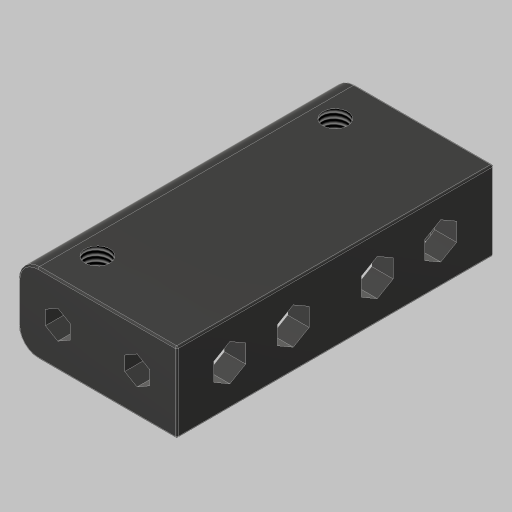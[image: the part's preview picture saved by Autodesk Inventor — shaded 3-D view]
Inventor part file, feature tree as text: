
AUTODESK INVENTOR PART (.ipt)
format: ipt  version: 2023.5 (Build 275446000, 446)  size: 305,664 bytes
history: native  units: in
note: dims shown in document units (in); Inventor stores cm internally (conversion verified against a paired STEP export)
features: sketch x5, extrude x4, fillet x3, projected_geometry x2, hole x1
ambient origin geometry x8: Origin, YZ Plane, XZ Plane, XY Plane, X Axis, Y Axis, Z Axis, Center Point
bodies: Solid1 (feature_tree)
feature tree (15):
  extrude  "Extrusion1"  Depth=0.5in
  hole  "Hole1"  [1 undecoded]
  fillet  "Fillet1"  Radius=0.25in
  fillet  "Fillet2"  Radius=0.125in
  extrude  "Extrusion2"  Depth=0.125in
  fillet  "Fillet3"  Radius=0.125in
  extrude  "Extrusion3"  Depth=0.375in TaperAngle=0.0deg
  extrude  "Extrusion4"  Depth=0.13in
  sketch  "Sketch1"  dims[d0=1.0in d1=0.5in]
  sketch  "Sketch2"  dims[d2=2.0in d3=0.0in d4=1.5in d5=0.25in]
  sketch  "Sketch3"  dims[d6=0.156in d7=0.38in d8=0.385in d9=0.25in d10=0.5635in d11=1.0in d12=0.8108in d13=0.125in]
  sketch  "Sketch4"  dims[d14=0.01in d15=0.125in d16=0.125in]
  sketch  "Sketch5"  dims[d17=0.125in d18=0.375in d19=0.0in d20=0.13in d21=0.2in d23=0.7874in d25=0.4in d26=0.3937in d28=1.0in d30=0.0in d31=0.0in d32=0.25in d33=0.0in d34=0.0in d35=0.265in d36=0.0344in d37=0.5in d38=0.0344in]
  projected_geometry  "Project Cut Edges1"
  projected_geometry  "Project Cut Edges2"
note: 1 required parameter value undecoded (feature->parameter linkage not recoverable at this tier; creation-order binding heuristic only, values carry confidence <= 0.55)
